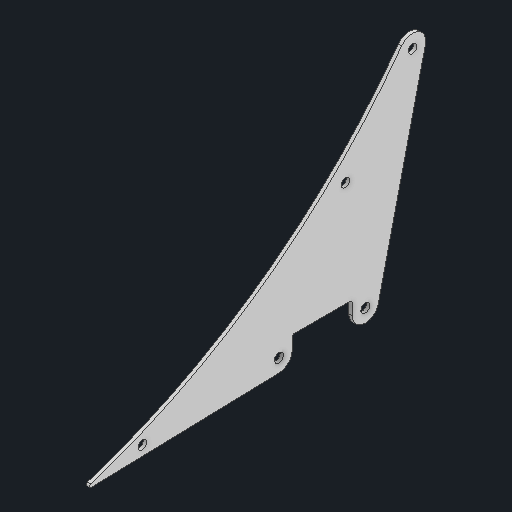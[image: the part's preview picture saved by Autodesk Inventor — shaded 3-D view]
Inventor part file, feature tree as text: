
AUTODESK INVENTOR PART (.ipt)
format: ipt  version: 2025 (Build 290162000, 162)  size: 116,736 bytes
history: native  units: in
note: dims shown in document units (in); Inventor stores cm internally (conversion verified against a paired STEP export)
features: other x3, extrude x1, sketch x1
ambient origin geometry x8: Origin, YZ Plane, XZ Plane, XY Plane, X Axis, Y Axis, Z Axis, Center Point
bodies: Solid1 (feature_tree)
feature tree (5):
  other  "Blocks"
  extrude  "Extrusion1"  Depth=0.25in
  sketch  "Sketch1"  dims[d3=0.0625in d4=0.0in d7=0.5in d8=0.164in d9=0.25in d11=0.0312in d13=0.164in d15=0.5in d16=0.0312in]
  other  "main"
  other  "main:1"
